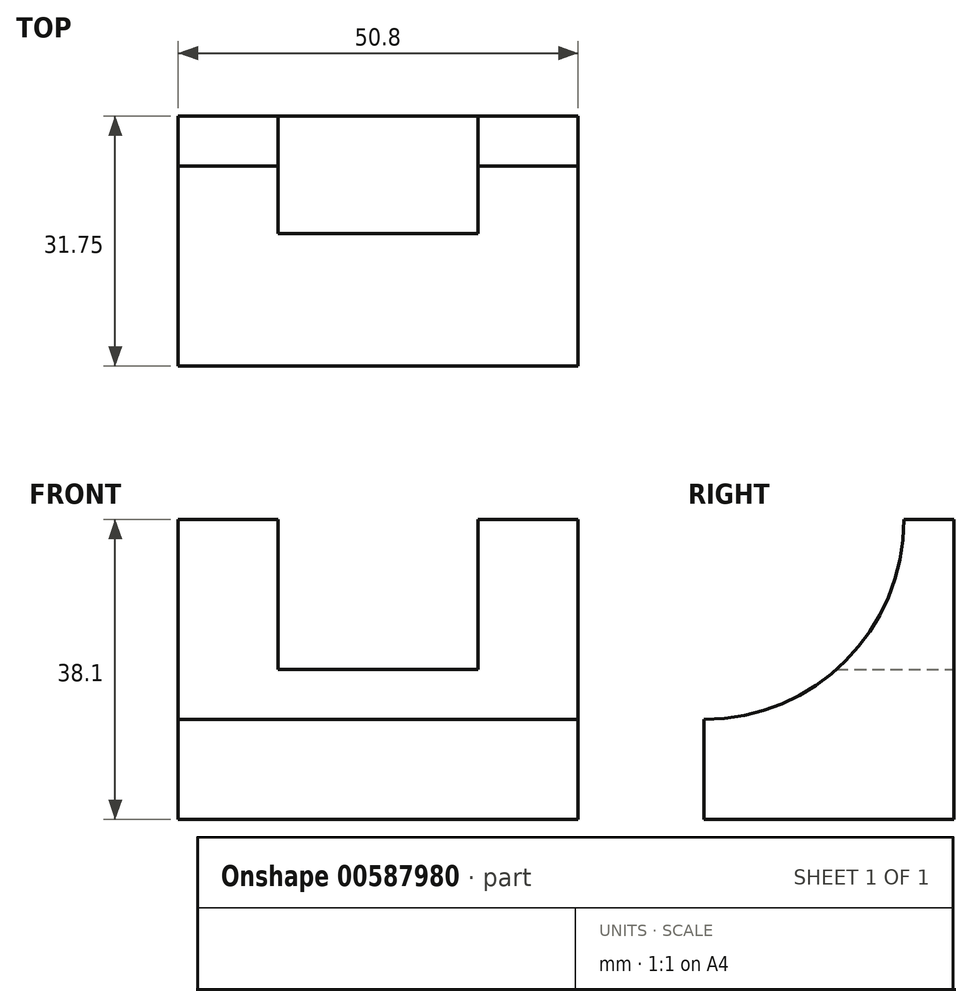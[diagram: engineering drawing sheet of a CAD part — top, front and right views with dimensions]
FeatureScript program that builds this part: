
annotation { "Feature Type Name" : "Feature", "Feature Type Description" : "" }
export const myFeature = defineFeature(function(context is Context, id is Id, definition is map)
    precondition{}
    {
        {
            var Q0;
            Q0=qCreatedBy(makeId("Front.planeOp"),FACE);
            var sketch = newSketch(context, id + "F0", { "sketchPlane" : qUnion([Q0])});
            skLineSegment(sketch, "E0.bottom", {"start": v(-70.61, 49.42) * mm, "end": v(-19.81, 49.42) * mm});
            skLineSegment(sketch, "E0.top", {"start": v(-70.61, 11.32) * mm, "end": v(-19.81, 11.32) * mm});
            skLineSegment(sketch, "E0.left", {"start": v(-70.61, 49.42) * mm, "end": v(-70.61, 11.32) * mm});
            skLineSegment(sketch, "E0.right", {"start": v(-19.81, 49.42) * mm, "end": v(-19.81, 11.32) * mm});
            skSolve(sketch);
        }
        {
            var Q0;
            Q0 = qSketchRegion(id + "F0", true);
            extrude(context, id + "F1", {"entities" : qUnion([Q0]), "depth" : 31.75 * mm, "offsetDistance" : 25.4 * mm});
        }
        {
            var Q0;
            Q0=makeQuery(id+"F1.opExtrude","SWEPT_FACE",FACE,{"disambiguationData":[OSD([sQuery(id+"F0.wireOp",EDGE,"E0.right")])]});
            var sketch = newSketch(context, id + "F2", { "sketchPlane" : qUnion([Q0])});
            skArc(sketch, "E1", {"start": v(-31.75, 24.02) * mm, "mid": v(-13.79, 31.46) * mm, "end": v(-6.35, 49.42) * mm});
            skSolve(sketch);
        }
        {
            var Q0;
            {var subQ0=sQuery(id+"F2.wireOp",EDGE,"E1");Q0=makeQuery(id+"F2.imprint","IMPRINT",FACE,{"disambiguationData":[TD([[makeQuery(id+"F2.imprint","IMPRINT",EDGE,{"derivedFrom":subQ0}),1.0]])]});}
            extrude(context, id + "F3", {"entities" : qUnion([Q0]), "operationType" : NewBodyOperationType.REMOVE, "endBound" : BoundingType.THROUGH_ALL, "oppositeDirection" : true, "depth" : 25.4 * mm, "offsetDistance" : 25.4 * mm});
        }
        {
            var Q0;
            Q0=makeQuery(id+"F1.opExtrude","CAP_FACE",FACE,{"disambiguationData":[OSD([sQuery(id+"F0.wireOp",EDGE,"E0.bottom"),sQuery(id+"F0.wireOp",EDGE,"E0.top"),sQuery(id+"F0.wireOp",EDGE,"E0.left"),sQuery(id+"F0.wireOp",EDGE,"E0.right")])],"isStart":true});
            var sketch = newSketch(context, id + "F4", { "sketchPlane" : qUnion([Q0])});
            skLineSegment(sketch, "E2.bottom", {"start": v(32.51, 49.42) * mm, "end": v(57.91, 49.42) * mm});
            skLineSegment(sketch, "E2.top", {"start": v(32.51, 30.37) * mm, "end": v(57.91, 30.37) * mm});
            skLineSegment(sketch, "E2.left", {"start": v(32.51, 49.42) * mm, "end": v(32.51, 30.37) * mm});
            skLineSegment(sketch, "E2.right", {"start": v(57.91, 49.42) * mm, "end": v(57.91, 30.37) * mm});
            skSolve(sketch);
        }
        {
            var Q0;
            Q0 = qSketchRegion(id + "F4", true);
            extrude(context, id + "F5", {"entities" : qUnion([Q0]), "operationType" : NewBodyOperationType.REMOVE, "oppositeDirection" : true, "depth" : 25.4 * mm, "offsetDistance" : 25.4 * mm});
        }
    });
